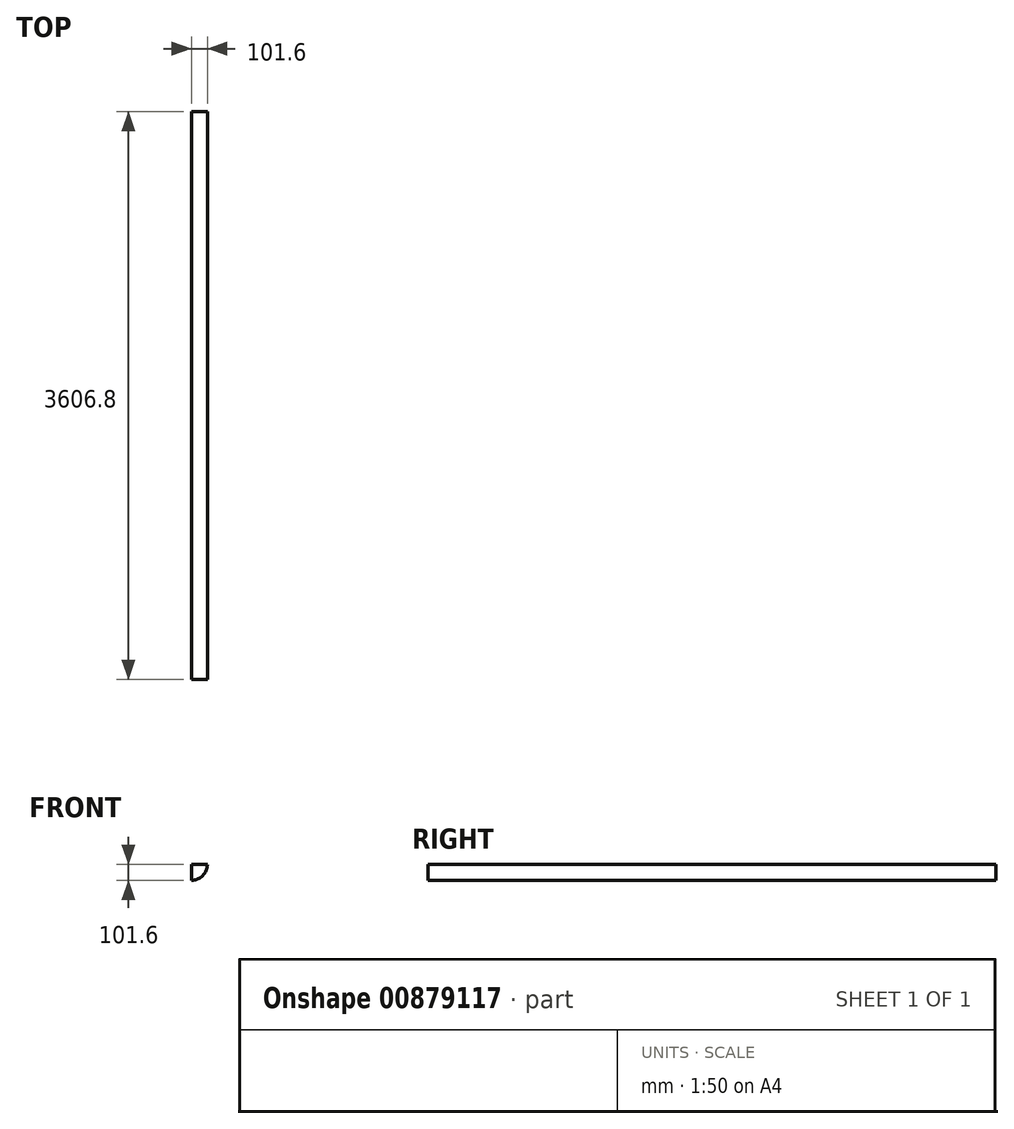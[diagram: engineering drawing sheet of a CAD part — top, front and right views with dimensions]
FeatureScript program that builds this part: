
annotation { "Feature Type Name" : "Feature", "Feature Type Description" : "" }
export const myFeature = defineFeature(function(context is Context, id is Id, definition is map)
    precondition{}
    {
        {
            var Q0;
            Q0=qCreatedBy(makeId("Front.planeOp"),FACE);
            var sketch = newSketch(context, id + "F0", { "sketchPlane" : qUnion([Q0])});
            skArc(sketch, "E0", {"start": v(0, -101.6) * mm, "mid": v(71.84, -71.84) * mm, "end": v(101.6, 0) * mm});
            skLineSegment(sketch, "E1", {"start": v(0, 0) * mm, "end": v(101.6, 0) * mm});
            skLineSegment(sketch, "E2", {"start": v(0, 0) * mm, "end": v(0, -101.6) * mm});
            skSolve(sketch);
        }
        {
            var Q0;
            Q0 = qSketchRegion(id + "F0", true);
            extrude(context, id + "F1", {"entities" : qUnion([Q0]), "depth" : 3606.8 * mm, "offsetDistance" : 25.4 * mm});
        }
    });
